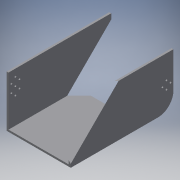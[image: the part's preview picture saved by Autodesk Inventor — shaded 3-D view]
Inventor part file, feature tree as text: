
AUTODESK INVENTOR PART (.ipt)
format: ipt  version: 2016 (Build 200138000, 138)  size: 137,728 bytes
history: native  units: in
note: dims shown in document units (in); Inventor stores cm internally (conversion verified against a paired STEP export)
features: reference x12, sketch x5, extrude x3, hole x2, fillet x1
ambient origin geometry x8: Origin, YZ Plane, XZ Plane, XY Plane, X Axis, Y Axis, Z Axis, Center Point
bodies: Solid1 (feature_tree)
feature tree (23):
  extrude  "Extrusion1"  Depth=8.0in
  extrude  "Extrusion2"  Depth=4.7in
  extrude  "Extrusion3"  Depth=2.5in
  fillet  "Fillet1"  Radius=0.15in
  hole  "Hole2"  [1 undecoded]
  hole  "Hole3"  [1 undecoded]
  sketch  "Sketch1"  dims[d0=5.0in d1=8.0in]
  sketch  "Sketch3"  dims[d2=4.0in d3=0.0in d4=4.7in]
  sketch  "Sketch4"  dims[d5=3.85in d6=0.0in d7=2.5in d8=0.15in d9=0.0in]
  sketch  "Sketch6"  dims[d10=1.2in]
  reference  "Reference1"
  reference  "Reference2"
  reference  "Reference3"
  reference  "Reference4"
  reference  "Reference5"
  reference  "Reference6"
  reference  "Reference7"
  sketch  "Sketch7"  dims[d18=0.1457in d19=0.75in d20=0.375in d21=0.25in d22=0.5635in d23=0.15in d24=0.0in d25=0.1457in d26=0.75in d27=0.375in d28=0.25in d29=0.5635in d30=0.15in d31=0.0in]
  reference  "Reference13"
  reference  "Reference14"
  reference  "Reference15"
  reference  "Reference16"
  reference  "Reference17"
note: 2 required parameter values undecoded (feature->parameter linkage not recoverable at this tier; creation-order binding heuristic only, values carry confidence <= 0.55)
